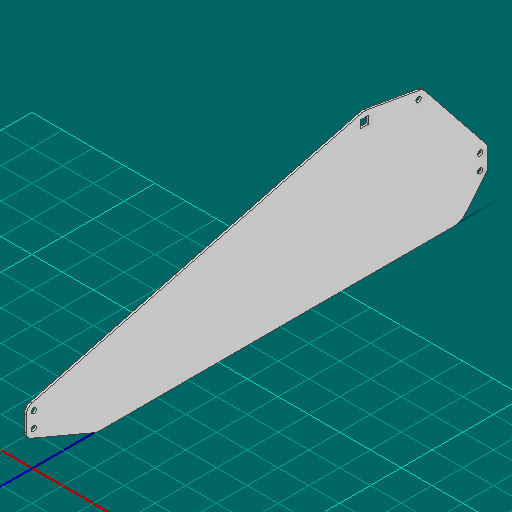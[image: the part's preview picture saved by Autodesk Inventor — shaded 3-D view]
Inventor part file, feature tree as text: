
AUTODESK INVENTOR PART (.ipt)
format: ipt  version: 2025 (Build 290162000, 162)  size: 144,384 bytes
history: native  units: in
note: dims shown in document units (in); Inventor stores cm internally (conversion verified against a paired STEP export)
features: other x4, extrude x1, sketch x1
ambient origin geometry x8: Origin, YZ Plane, XZ Plane, XY Plane, X Axis, Y Axis, Z Axis, Center Point
bodies: Solid1 (feature_tree)
feature tree (6):
  other  "Blocks"
  extrude  "Extrusion1"  Depth=0.0625in TaperAngle=0.0deg
  sketch  "Sketch1"  dims[d0=0.5in d1=0.5in d2=1.0in d3=0.0625in d4=0.0in d6=0.5in d7=1.0in d8=0.2485in d9=0.2485in d10=0.625in]
  other  "maiin"
  other  "main"
  other  "main:1"
